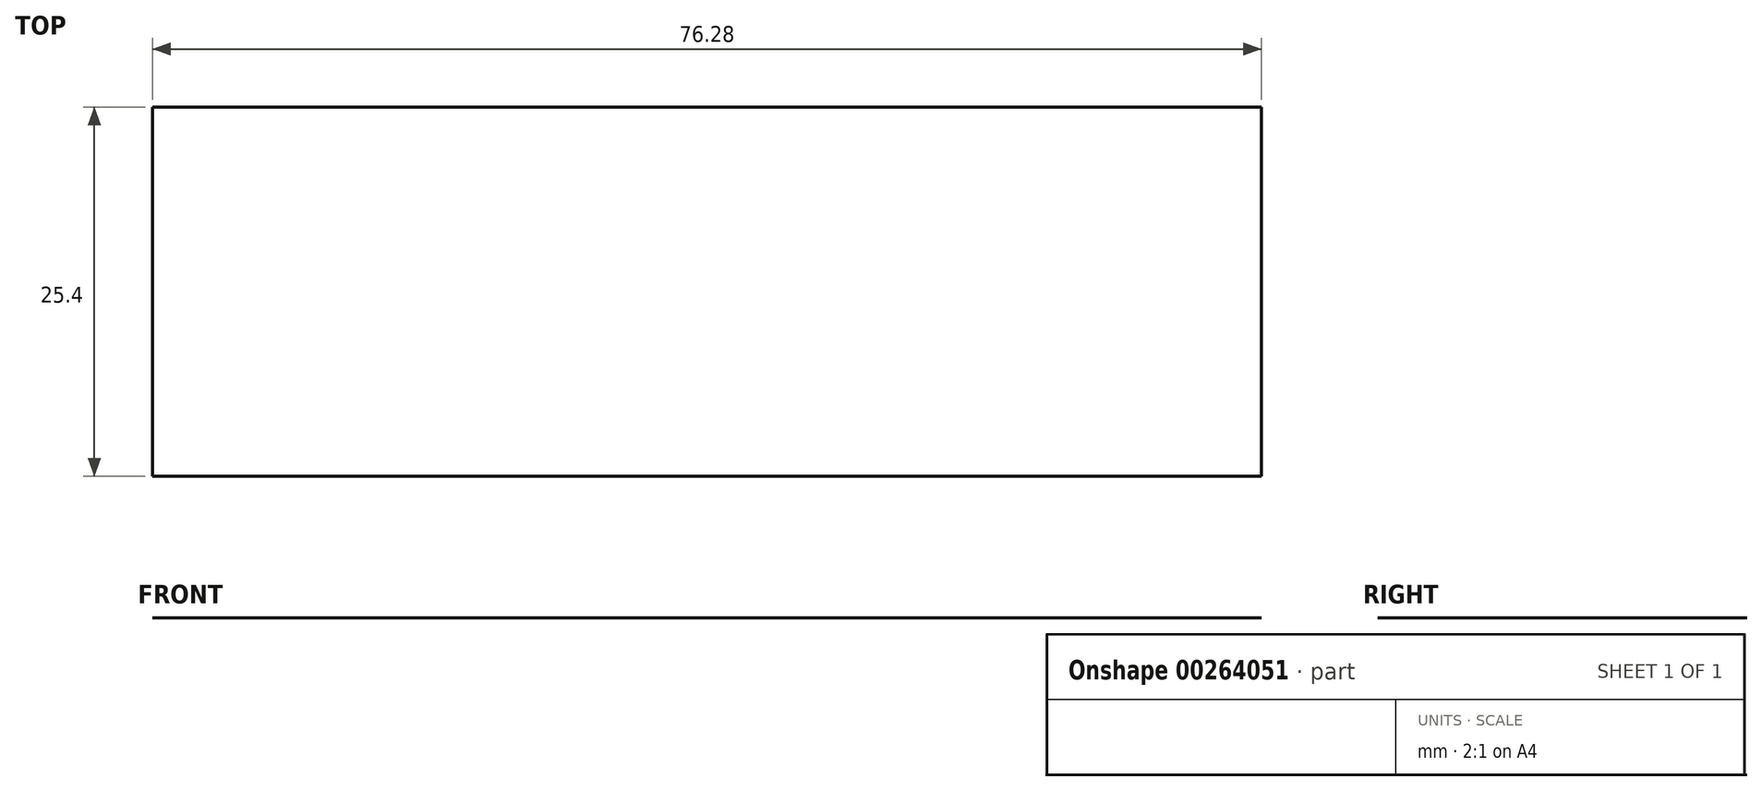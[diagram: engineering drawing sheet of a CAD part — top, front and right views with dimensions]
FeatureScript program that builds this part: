
annotation { "Feature Type Name" : "Feature", "Feature Type Description" : "" }
export const myFeature = defineFeature(function(context is Context, id is Id, definition is map)
    precondition{}
    {
        {
            var Q0;
            Q0=qCreatedBy(makeId("Front.planeOp"),FACE);
            var sketch = newSketch(context, id + "F0", { "sketchPlane" : qUnion([Q0])});
            skLineSegment(sketch, "E0", {"start": v(-86.92, 44.9) * mm, "end": v(-86.92, 44.9) * mm});
            skLineSegment(sketch, "E1", {"start": v(-86.92, 44.9) * mm, "end": v(-86.92, -6.1) * mm});
            skLineSegment(sketch, "E2", {"start": v(-86.92, -6.1) * mm, "end": v(65.63, -6.1) * mm});
            skLineSegment(sketch, "E3", {"start": v(-86.92, 44.9) * mm, "end": v(-10.64, 44.9) * mm});
            skLineSegment(sketch, "E4", {"start": v(-10.64, 44.9) * mm, "end": v(-10.64, 18.94) * mm});
            skLineSegment(sketch, "E5", {"start": v(-10.64, 18.94) * mm, "end": v(-86.92, 18.94) * mm});
            skLineSegment(sketch, "E6", {"start": v(65.63, -6.1) * mm, "end": v(65.63, 17.78) * mm});
            skLineSegment(sketch, "E7", {"start": v(65.63, 17.78) * mm, "end": v(-10.64, 18.94) * mm});
            skSolve(sketch);
        }
        {
            var Q0;
            Q0=sQuery(id+"F0.wireOp",EDGE,"E5");
            extrude(context, id + "F1", {"bodyType" : ToolBodyType.SURFACE, "surfaceEntities" : qUnion([Q0]), "depth" : 25.4 * mm});
        }
    });
